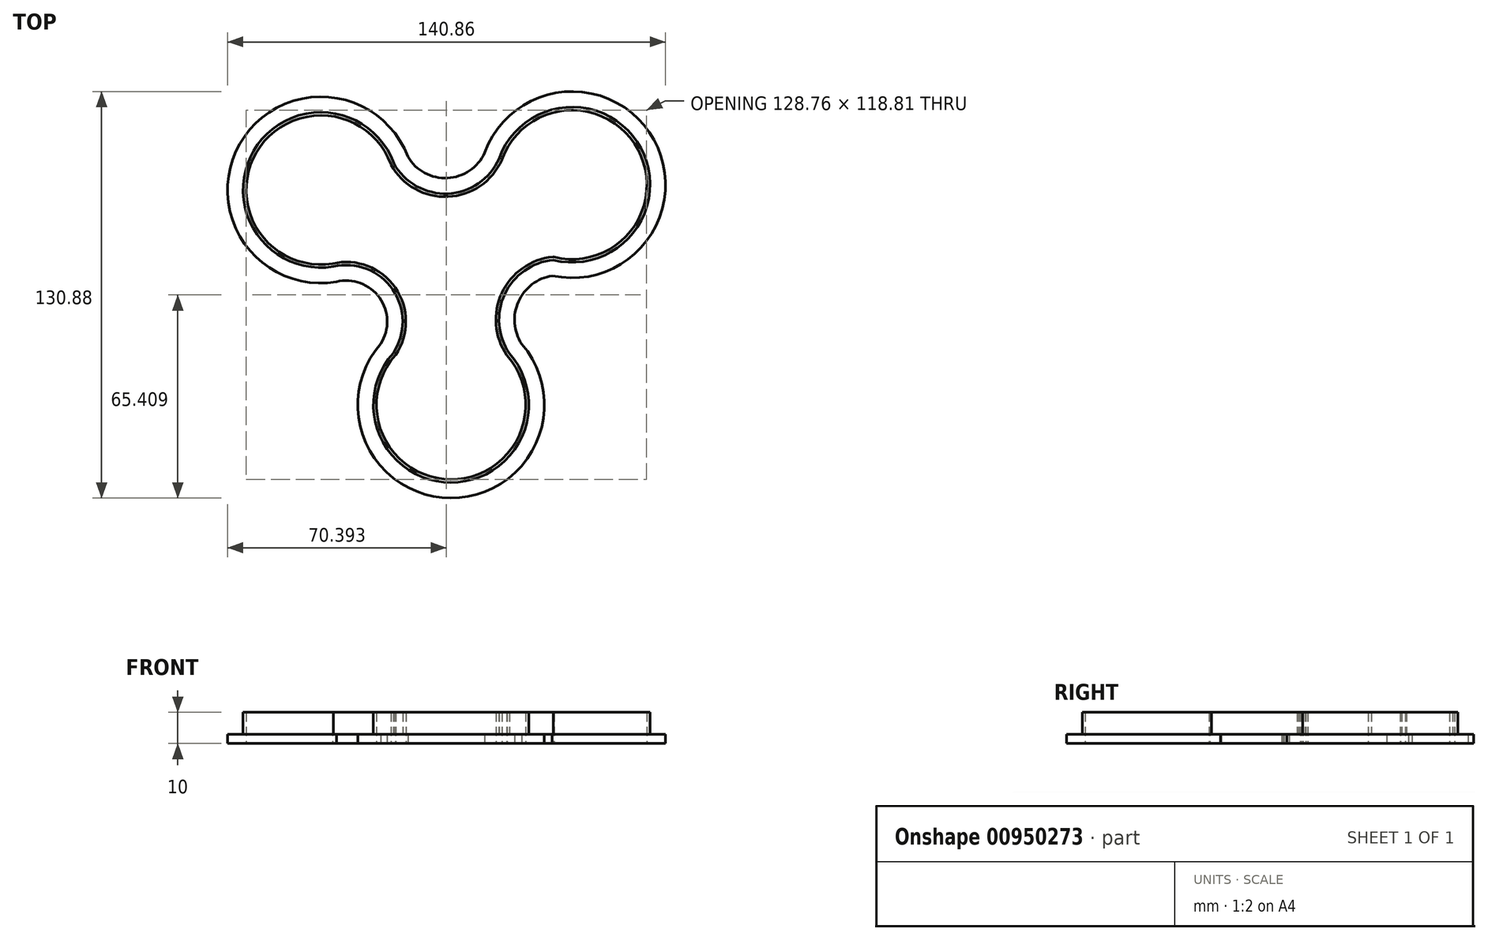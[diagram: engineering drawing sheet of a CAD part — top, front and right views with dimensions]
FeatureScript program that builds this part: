
annotation { "Feature Type Name" : "Feature", "Feature Type Description" : "" }
export const myFeature = defineFeature(function(context is Context, id is Id, definition is map)
    precondition{}
    {
        {
            var Q0;
            Q0=qCreatedBy(makeId("Top.planeOp"),FACE);
            var sketch = newSketch(context, id + "F0", { "sketchPlane" : qUnion([Q0])});
            skPoint(sketch, "E0.center", {"position": v(0, 0) * mm});
            skArc(sketch, "E1.0", {"start": v(-17.44, 31.1) * mm, "mid": v(-62.5, 35.12) * mm, "end": v(-36.9, -2.18) * mm});
            skArc(sketch, "E2.0", {"start": v(33.8, -0.05) * mm, "mid": v(62, 35.96) * mm, "end": v(16.4, 32.6) * mm});
            skArc(sketch, "E3.0", {"start": v(-17.64, -30) * mm, "mid": v(0.87, -71.69) * mm, "end": v(19.74, -30.17) * mm});
            skArc(sketch, "E4", {"start": v(-17.64, -30) * mm, "mid": v(-17.81, -9.54) * mm, "end": v(-36.9, -2.18) * mm});
            skArc(sketch, "E5", {"start": v(-17.44, 31.1) * mm, "mid": v(-0.06, 21.31) * mm, "end": v(16.4, 32.6) * mm});
            skArc(sketch, "E6", {"start": v(33.8, -0.05) * mm, "mid": v(18.2, -11.1) * mm, "end": v(19.74, -30.17) * mm});
            skArc(sketch, "E7.0", {"start": v(-12.9, 33.2) * mm, "mid": v(-0.19, 26.31) * mm, "end": v(11.76, 34.46) * mm});
            skArc(sketch, "E7.1", {"start": v(-21.63, -26.96) * mm, "mid": v(-22.06, -12.2) * mm, "end": v(-35.92, -7.08) * mm});
            skArc(sketch, "E7.2", {"start": v(-21.63, -26.96) * mm, "mid": v(0.87, -76.69) * mm, "end": v(23.72, -27.13) * mm});
            skArc(sketch, "E7.3", {"start": v(-12.9, 33.2) * mm, "mid": v(-66.97, 37.38) * mm, "end": v(-35.92, -7.08) * mm});
            skArc(sketch, "E7.4", {"start": v(33.54, -5.12) * mm, "mid": v(22.63, -13.45) * mm, "end": v(23.72, -27.13) * mm});
            skArc(sketch, "E7.5", {"start": v(33.54, -5.12) * mm, "mid": v(66.23, 38.65) * mm, "end": v(11.76, 34.46) * mm});
            skArc(sketch, "E8.0", {"start": v(-18.38, 30.75) * mm, "mid": v(-61.63, 34.63) * mm, "end": v(-37.1, -1.2) * mm});
            skArc(sketch, "E9.0", {"start": v(-18.32, 30.6) * mm, "mid": v(-0.01, 20.31) * mm, "end": v(17.31, 32.2) * mm});
            skArc(sketch, "E10.0", {"start": v(34.05, 0.92) * mm, "mid": v(61.12, 35.48) * mm, "end": v(17.34, 32.26) * mm});
            skArc(sketch, "E11.0", {"start": v(33.7, 0.95) * mm, "mid": v(17.3, -10.68) * mm, "end": v(18.91, -30.73) * mm});
            skArc(sketch, "E12.0", {"start": v(-16.9, -30.67) * mm, "mid": v(0.87, -70.69) * mm, "end": v(19, -30.83) * mm});
            skArc(sketch, "E13.0", {"start": v(-16.8, -30.56) * mm, "mid": v(-16.98, -8.98) * mm, "end": v(-37.1, -1.2) * mm});
            skLineSegment(sketch, "E14", {"start": v(33.7, 0.95) * mm, "end": v(34.05, 0.92) * mm});
            skLineSegment(sketch, "E15", {"start": v(-18.38, 30.75) * mm, "end": v(-18.32, 30.6) * mm});
            skLineSegment(sketch, "E16", {"start": v(-16.9, -30.67) * mm, "end": v(-16.8, -30.56) * mm});
            skLineSegment(sketch, "E17", {"start": v(18.91, -30.73) * mm, "end": v(19, -30.83) * mm});
            skLineSegment(sketch, "E18", {"start": v(17.34, 32.26) * mm, "end": v(17.31, 32.2) * mm});
            skPoint(sketch, "E19.end.orphan", {"position": v(17.34, 32.26) * mm});
            skSolve(sketch);
        }
        {
            var Q0;
            Q0=makeQuery(id+"F0.imprint","IMPRINT",FACE,{"disambiguationData":[TD([[makeQuery(id+"F0.imprint","IMPRINT",EDGE,{"derivedFrom":sQuery(id+"F0.wireOp",EDGE,"E1.0")}),-1.0]])]});
            extrude(context, id + "F1", {"entities" : qUnion([Q0]), "depth" : 3 * mm, "offsetDistance" : 25 * mm});
        }
        {
            var Q0;
            Q0=makeQuery(id+"F0.imprint","IMPRINT",FACE,{"disambiguationData":[TD([[makeQuery(id+"F0.imprint","IMPRINT",EDGE,{"derivedFrom":sQuery(id+"F0.wireOp",EDGE,"E1.0")}),1.0]])]});
            extrude(context, id + "F2", {"entities" : qUnion([Q0]), "operationType" : NewBodyOperationType.ADD, "depth" : 10 * mm, "offsetDistance" : 25 * mm});
        }
    });
